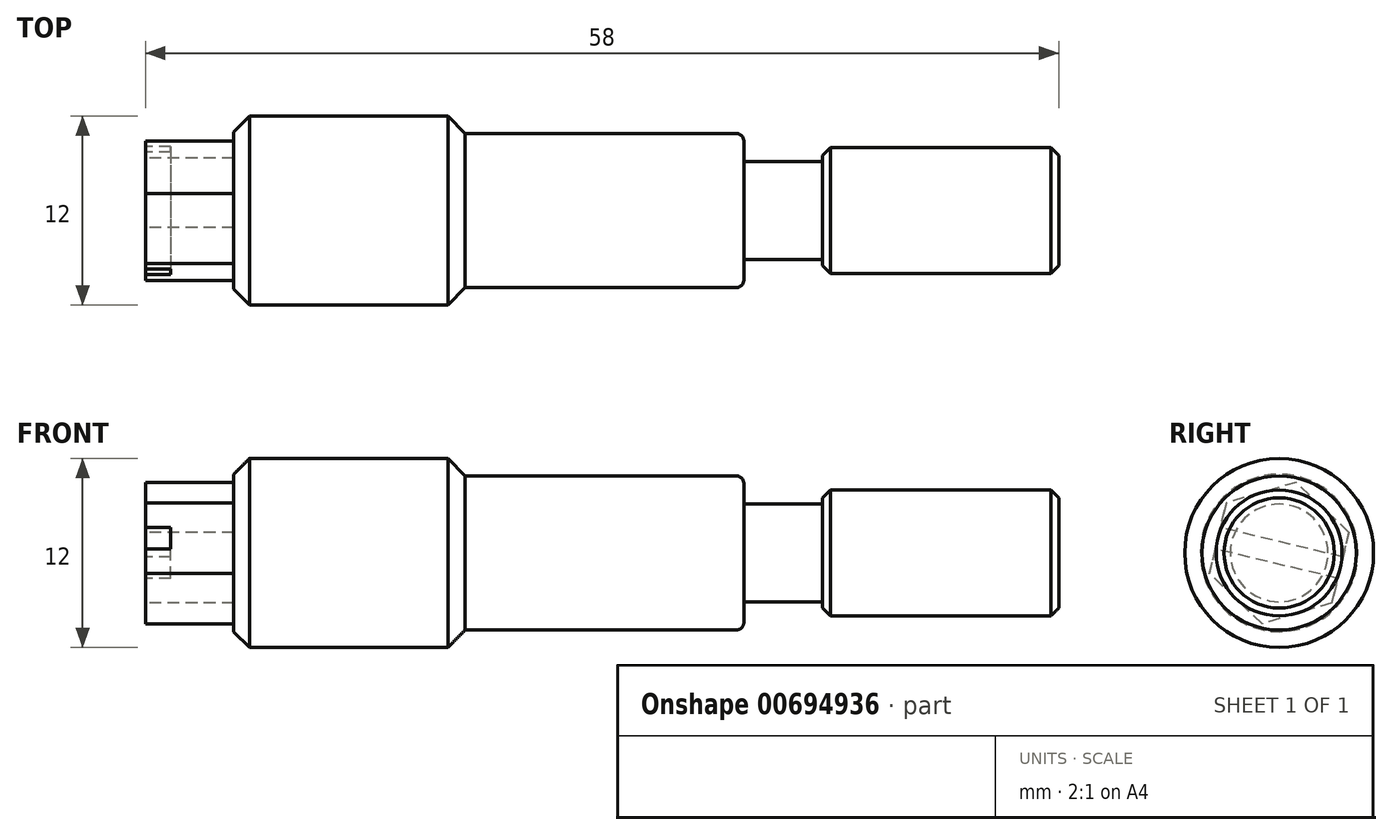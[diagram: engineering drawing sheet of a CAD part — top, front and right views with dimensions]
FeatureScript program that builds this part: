
annotation { "Feature Type Name" : "Feature", "Feature Type Description" : "" }
export const myFeature = defineFeature(function(context is Context, id is Id, definition is map)
    precondition{}
    {
        {
            var Q0;
            Q0=qCreatedBy(makeId("Front.planeOp"),FACE);
            var sketch = newSketch(context, id + "F0", { "sketchPlane" : qUnion([Q0])});
            skLineSegment(sketch, "E0", {"start": v(0, 0) * mm, "end": v(0, 4) * mm});
            skLineSegment(sketch, "E1", {"start": v(0, 4) * mm, "end": v(-15, 4) * mm});
            skLineSegment(sketch, "E2", {"start": v(-15, 4) * mm, "end": v(-15, 3.1) * mm});
            skLineSegment(sketch, "E3", {"start": v(-15, 3.1) * mm, "end": v(-20, 3.1) * mm});
            skLineSegment(sketch, "E4", {"start": v(-20, 3.1) * mm, "end": v(-20, 4.9) * mm});
            skLineSegment(sketch, "E5", {"start": v(-20, 4.9) * mm, "end": v(-37.7, 4.9) * mm});
            skLineSegment(sketch, "E6", {"start": v(-37.7, 4.9) * mm, "end": v(-37.7, 6) * mm});
            skLineSegment(sketch, "E7", {"start": v(-37.7, 6) * mm, "end": v(-52.4, 6) * mm});
            skLineSegment(sketch, "E8", {"start": v(17.65, 0) * mm, "end": v(-80.43, 0) * mm, "construction": true});
            skLineSegment(sketch, "E9", {"start": v(-52.4, 6) * mm, "end": v(-52.4, 5) * mm});
            skLineSegment(sketch, "E10", {"start": v(-52.4, 5) * mm, "end": v(-58, 5) * mm});
            skLineSegment(sketch, "E11", {"start": v(-58, 5) * mm, "end": v(-58, 0) * mm});
            skLineSegment(sketch, "E12", {"start": v(-58, 0) * mm, "end": v(0, 0) * mm});
            skSolve(sketch);
        }
        {
            var Q0;
            Q0 = qSketchRegion(id + "F0", true);
            var Q1;
            Q1=sQuery(id+"F0.wireOp",EDGE,"E8");
            revolve(context, id + "F1", {"entities" : qUnion([Q0]), "axis" : qUnion([Q1]), "revolveType" : RevolveType.FULL});
        }
        {
            var Q0;
            Q0=makeQuery(id+"F1.opRevolve","SWEPT_FACE",FACE,{"disambiguationData":[OSD([sQuery(id+"F0.wireOp",EDGE,"E11")])]});
            var sketch = newSketch(context, id + "F2", { "sketchPlane" : qUnion([Q0])});
            skCircle(sketch, "E13.cCircle", {"center": v(0, 0) * mm, "radius": 4 * mm, "construction": true});
            skLineSegment(sketch, "E13.0", {"start": v(3.35, 3.18) * mm, "end": v(4.43, -1.31) * mm});
            skLineSegment(sketch, "E13.1", {"start": v(4.43, -1.31) * mm, "end": v(1.08, -4.5) * mm});
            skLineSegment(sketch, "E13.2", {"start": v(1.08, -4.5) * mm, "end": v(-3.35, -3.18) * mm});
            skLineSegment(sketch, "E13.3", {"start": v(-3.35, -3.18) * mm, "end": v(-4.43, 1.31) * mm});
            skLineSegment(sketch, "E13.4", {"start": v(-4.43, 1.31) * mm, "end": v(-1.08, 4.5) * mm});
            skLineSegment(sketch, "E13.5", {"start": v(-1.08, 4.5) * mm, "end": v(3.35, 3.18) * mm});
            skPoint(sketch, "E13.0.midPoint", {"position": v(3.89, 0.93) * mm});
            skCircle(sketch, "E14", {"center": v(0, 0) * mm, "radius": 8.47 * mm});
            skSolve(sketch);
        }
        {
            var Q0;
            Q0 = qSketchRegion(id + "F2", true);
            var Q1;
            Q1=makeQuery(id+"F1.opRevolve","SWEPT_FACE",FACE,{"disambiguationData":[OSD([sQuery(id+"F0.wireOp",EDGE,"E9")])]});
            extrude(context, id + "F3", {"entities" : qUnion([Q0]), "operationType" : NewBodyOperationType.REMOVE, "endBound" : BoundingType.UP_TO_SURFACE, "oppositeDirection" : true, "depth" : 5 * mm, "endBoundEntityFace" : qUnion([Q1]), "offsetDistance" : 25 * mm});
        }
        {
            var Q0;
            Q0=makeQuery(id+"F1.opRevolve","SWEPT_EDGE",EDGE,{"disambiguationData":[OSD([sQuery(id+"F0.wireOp",EDGE,"E6"),sQuery(id+"F0.wireOp",EDGE,"E7")])]});
            chamfer(context, id + "F4", {"entities" : qUnion([Q0]), "width" : 1.1 * mm, "tangentPropagation" : true});
        }
        {
            var Q0;
            Q0=makeQuery(id+"F1.opRevolve","SWEPT_EDGE",EDGE,{"disambiguationData":[OSD([sQuery(id+"F0.wireOp",EDGE,"E7"),sQuery(id+"F0.wireOp",EDGE,"E9")])]});
            chamfer(context, id + "F5", {"entities" : qUnion([Q0]), "width" : 1 * mm, "tangentPropagation" : true});
        }
        {
            var Q0;
            Q0=makeQuery(id+"F1.opRevolve","SWEPT_EDGE",EDGE,{"disambiguationData":[OSD([sQuery(id+"F0.wireOp",EDGE,"E0"),sQuery(id+"F0.wireOp",EDGE,"E1")])]});
            var Q1;
            Q1=makeQuery(id+"F1.opRevolve","SWEPT_EDGE",EDGE,{"disambiguationData":[OSD([sQuery(id+"F0.wireOp",EDGE,"E1"),sQuery(id+"F0.wireOp",EDGE,"E2")])]});
            chamfer(context, id + "F6", {"entities" : qUnion([Q0, Q1]), "width" : .5 * mm, "tangentPropagation" : true});
        }
        {
            var Q0;
            Q0=makeQuery(id+"F1.opRevolve","SWEPT_EDGE",EDGE,{"disambiguationData":[OSD([sQuery(id+"F0.wireOp",EDGE,"E4"),sQuery(id+"F0.wireOp",EDGE,"E5")])]});
            fillet(context, id + "F7", {"entities" : qUnion([Q0]), "radius" : .5 * mm, "tangentPropagation" : true, "allowEdgeOverflow" : false});
        }
        {
            var Q0;
            Q0=makeQuery(id+"F1.opRevolve","SWEPT_FACE",FACE,{"disambiguationData":[OSD([sQuery(id+"F0.wireOp",EDGE,"E11")])]});
            var sketch = newSketch(context, id + "F8", { "sketchPlane" : qUnion([Q0])});
            skLineSegment(sketch, "E15.0", {"start": v(-3.73, -1.62) * mm, "end": v(4.05, 0.25) * mm});
            skLineSegment(sketch, "E16.0", {"start": v(-4.05, -0.25) * mm, "end": v(3.73, 1.62) * mm});
            skLineSegment(sketch, "E17", {"start": v(-4.05, -0.25) * mm, "end": v(-3.73, -1.62) * mm});
            skLineSegment(sketch, "E18", {"start": v(4.05, 0.25) * mm, "end": v(3.73, 1.62) * mm});
            skPoint(sketch, "E19.end.orphan", {"position": v(3.89, 0.93) * mm});
            skPoint(sketch, "E19.start.orphan", {"position": v(-3.89, -0.93) * mm});
            skSolve(sketch);
        }
        {
            var Q0;
            Q0 = qSketchRegion(id + "F8", true);
            extrude(context, id + "F9", {"entities" : qUnion([Q0]), "operationType" : NewBodyOperationType.REMOVE, "oppositeDirection" : true, "depth" : 1.6 * mm, "offsetDistance" : 25 * mm});
        }
    });
